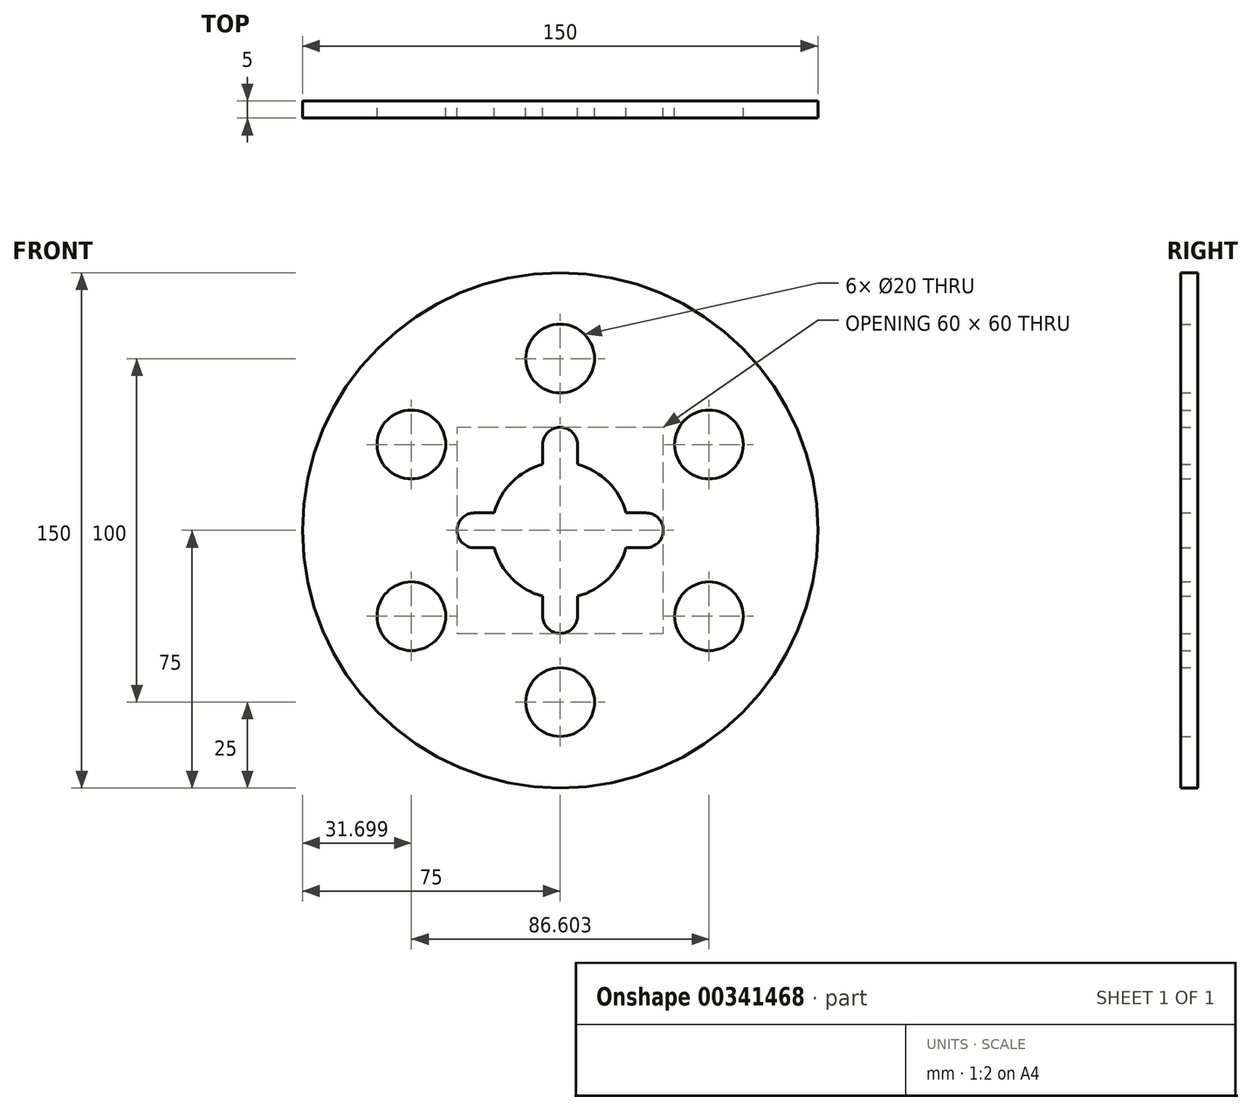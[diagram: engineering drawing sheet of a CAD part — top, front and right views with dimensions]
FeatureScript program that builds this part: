
annotation { "Feature Type Name" : "Feature", "Feature Type Description" : "" }
export const myFeature = defineFeature(function(context is Context, id is Id, definition is map)
    precondition{}
    {
        {
            var Q0;
            Q0=qCreatedBy(makeId("Front.planeOp"),FACE);
            var sketch = newSketch(context, id + "F0", { "sketchPlane" : qUnion([Q0])});
            skCircle(sketch, "E0", {"center": v(0, 0) * mm, "radius": 75 * mm});
            skArc(sketch, "E1", {"start": v(-5.08, 19.18) * mm, "mid": v(-14.03, 14.03) * mm, "end": v(-19.18, 5.08) * mm});
            skCircle(sketch, "E2", {"center": v(0, 0) * mm, "radius": 30 * mm, "construction": true});
            skArc(sketch, "E3", {"start": v(5.08, 24.92) * mm, "mid": v(0, 30) * mm, "end": v(-5.08, 24.92) * mm});
            skLineSegment(sketch, "E4", {"start": v(-5.08, 24.92) * mm, "end": v(-5.08, 19.18) * mm});
            skLineSegment(sketch, "E5", {"start": v(5.08, 24.92) * mm, "end": v(5.08, 19.18) * mm});
            skLineSegment(sketch, "E6.1.0", {"start": v(-24.92, -5.08) * mm, "end": v(-19.18, -5.08) * mm});
            skArc(sketch, "E6.1.1", {"start": v(-24.92, 5.08) * mm, "mid": v(-30, 0) * mm, "end": v(-24.92, -5.08) * mm});
            skLineSegment(sketch, "E6.1.2", {"start": v(-24.92, 5.08) * mm, "end": v(-19.18, 5.08) * mm});
            skLineSegment(sketch, "E6.2.0", {"start": v(5.08, -24.92) * mm, "end": v(5.08, -19.18) * mm});
            skArc(sketch, "E6.2.1", {"start": v(-5.08, -24.92) * mm, "mid": v(0, -30) * mm, "end": v(5.08, -24.92) * mm});
            skLineSegment(sketch, "E6.2.2", {"start": v(-5.08, -24.92) * mm, "end": v(-5.08, -19.18) * mm});
            skLineSegment(sketch, "E6.3.0", {"start": v(24.92, 5.08) * mm, "end": v(19.18, 5.08) * mm});
            skArc(sketch, "E6.3.1", {"start": v(24.92, -5.08) * mm, "mid": v(30, 0) * mm, "end": v(24.92, 5.08) * mm});
            skLineSegment(sketch, "E6.3.2", {"start": v(24.92, -5.08) * mm, "end": v(19.18, -5.08) * mm});
            skArc(sketch, "E7.trimOffspring", {"start": v(-19.18, -5.08) * mm, "mid": v(-14.03, -14.03) * mm, "end": v(-5.08, -19.18) * mm});
            skArc(sketch, "E8.trimOffspring", {"start": v(19.18, 5.08) * mm, "mid": v(14.03, 14.03) * mm, "end": v(5.08, 19.18) * mm});
            skArc(sketch, "E9.trimOffspring", {"start": v(5.08, -19.18) * mm, "mid": v(14.03, -14.03) * mm, "end": v(19.18, -5.08) * mm});
            skCircle(sketch, "E10", {"center": v(0, 0) * mm, "radius": 50 * mm, "construction": true});
            skCircle(sketch, "E11", {"center": v(0, 50) * mm, "radius": 10 * mm});
            skCircle(sketch, "E12.1.0", {"center": v(-43.3, 25) * mm, "radius": 10 * mm});
            skCircle(sketch, "E12.2.0", {"center": v(-43.3, -25) * mm, "radius": 10 * mm});
            skCircle(sketch, "E12.3.0", {"center": v(0, -50) * mm, "radius": 10 * mm});
            skCircle(sketch, "E12.4.0", {"center": v(43.3, -25) * mm, "radius": 10 * mm});
            skCircle(sketch, "E12.5.0", {"center": v(43.3, 25) * mm, "radius": 10 * mm});
            skSolve(sketch);
        }
        {
            var Q0;
            Q0=makeQuery(id+"F0.imprint","IMPRINT",FACE,{"disambiguationData":[TD([[makeQuery(id+"F0.imprint","IMPRINT",EDGE,{"derivedFrom":sQuery(id+"F0.wireOp",EDGE,"E0")}),1.0]])]});
            extrude(context, id + "F1", {"entities" : qUnion([Q0]), "depth" : 5 * mm});
        }
    });
